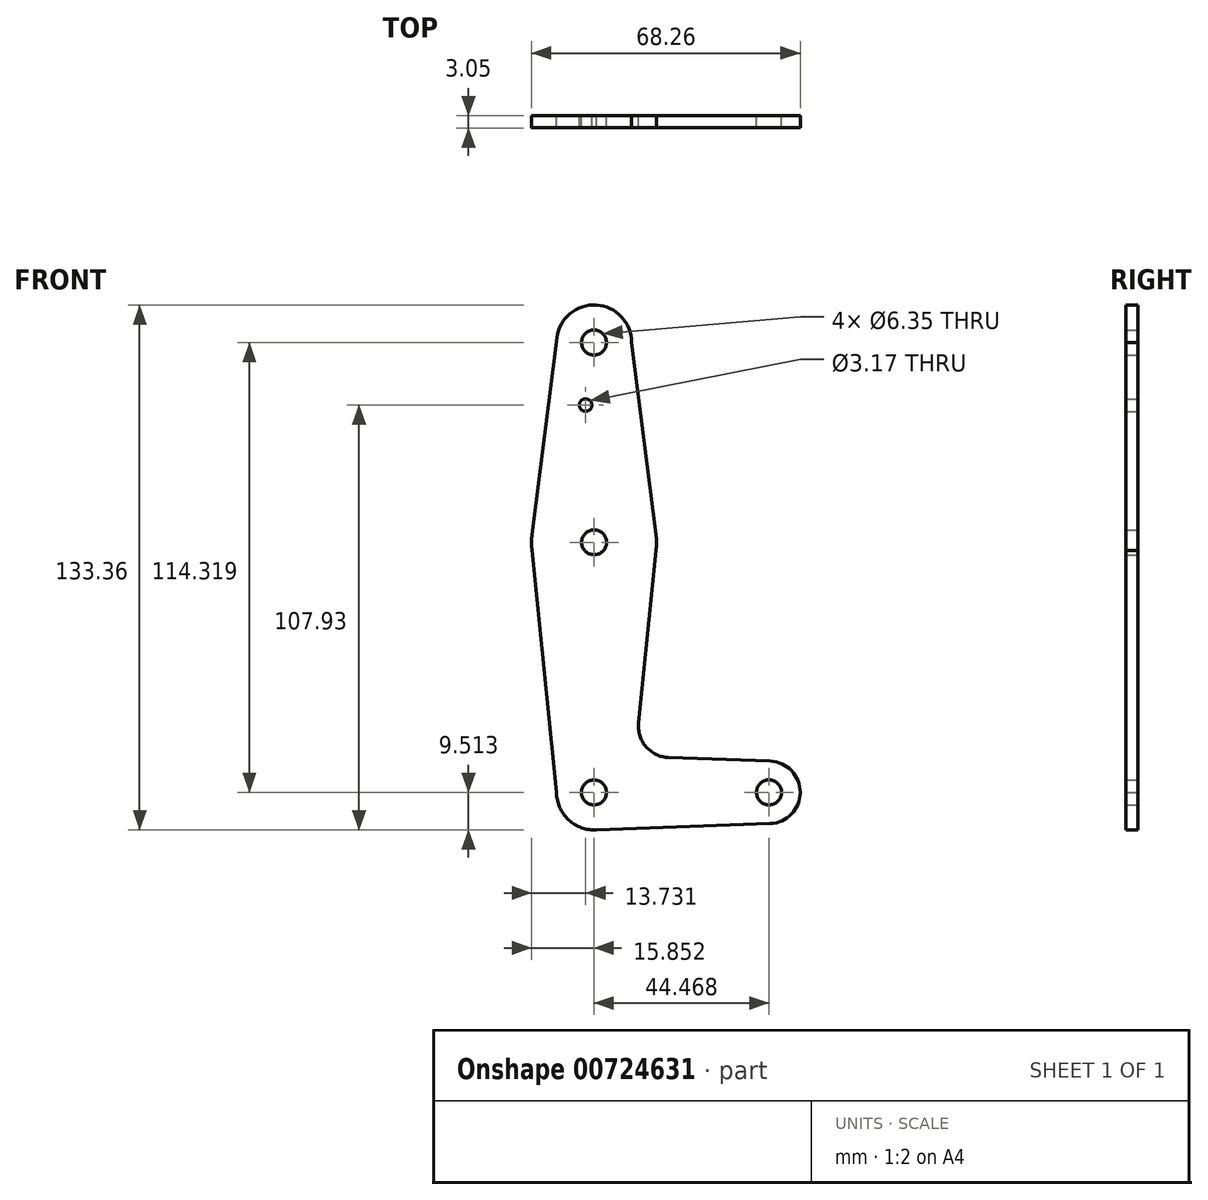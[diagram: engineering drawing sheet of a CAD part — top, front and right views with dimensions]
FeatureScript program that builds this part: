
annotation { "Feature Type Name" : "Feature", "Feature Type Description" : "" }
export const myFeature = defineFeature(function(context is Context, id is Id, definition is map)
    precondition{}
    {
        {
            var Q0;
            Q0=qCreatedBy(makeId("Front.planeOp"),FACE);
            var sketch = newSketch(context, id + "F0", { "sketchPlane" : qUnion([Q0])});
            skLineSegment(sketch, "E0", {"start": v(0, 114.3) * mm, "end": v(0, 0) * mm, "construction": true});
            skLineSegment(sketch, "E1", {"start": v(0, 0) * mm, "end": v(44.45, 0) * mm, "construction": true});
            skCircle(sketch, "E2", {"center": v(0, 114.3) * mm, "radius": 9.53 * mm});
            skCircle(sketch, "E3", {"center": v(0, 63.5) * mm, "radius": 15.88 * mm});
            skCircle(sketch, "E4", {"center": v(0, 0) * mm, "radius": 9.53 * mm});
            skCircle(sketch, "E5", {"center": v(44.45, 0) * mm, "radius": 7.94 * mm});
            skLineSegment(sketch, "E6", {"start": v(9.52, 114.3) * mm, "end": v(15.75, 65.5) * mm});
            skLineSegment(sketch, "E7", {"start": v(-9.45, 115.5) * mm, "end": v(-15.75, 65.48) * mm});
            skLineSegment(sketch, "E8", {"start": v(18.93, 8.85) * mm, "end": v(44.73, 7.93) * mm});
            skLineSegment(sketch, "E9", {"start": v(0, -9.53) * mm, "end": v(44.73, -7.93) * mm});
            skLineSegment(sketch, "E10", {"start": v(-9.52, 0) * mm, "end": v(-15.75, 61.52) * mm});
            skLineSegment(sketch, "E11", {"start": v(11.3, 17.6) * mm, "end": v(15.75, 61.5) * mm});
            skCircle(sketch, "E12", {"center": v(-2.14, 98.4) * mm, "radius": 1.59 * mm});
            skCircle(sketch, "E13", {"center": v(0.03, 63.53) * mm, "radius": 3.18 * mm});
            skArc(sketch, "E14.filletArc", {"start": v(11.3, 17.6) * mm, "mid": v(13.22, 11.57) * mm, "end": v(18.93, 8.85) * mm});
            skCircle(sketch, "E15", {"center": v(-0.02, -0.02) * mm, "radius": 3.18 * mm});
            skCircle(sketch, "E16", {"center": v(44.45, 0) * mm, "radius": 3.18 * mm});
            skCircle(sketch, "E17", {"center": v(0, 114.3) * mm, "radius": 3.18 * mm});
            skSolve(sketch);
        }
        {
            var Q0;
            Q0 = qSketchRegion(id + "F0", true);
            extrude(context, id + "F1", {"entities" : qUnion([Q0]), "depth" : 3.05 * mm, "offsetDistance" : 25.4 * mm});
        }
    });
